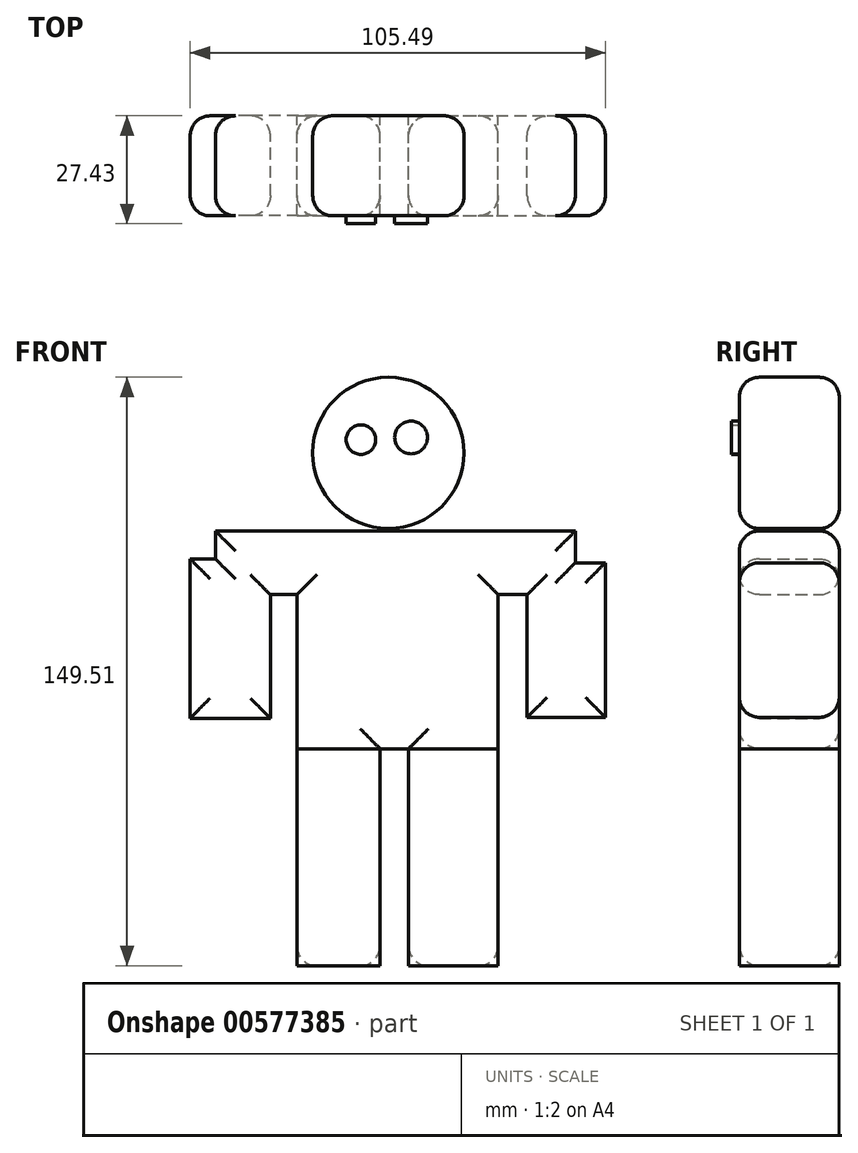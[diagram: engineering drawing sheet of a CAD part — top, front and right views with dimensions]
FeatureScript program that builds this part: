
annotation { "Feature Type Name" : "Feature", "Feature Type Description" : "" }
export const myFeature = defineFeature(function(context is Context, id is Id, definition is map)
    precondition{}
    {
        {
            var Q0;
            Q0=qCreatedBy(makeId("Front.planeOp"),FACE);
            var sketch = newSketch(context, id + "F0", { "sketchPlane" : qUnion([Q0])});
            skLineSegment(sketch, "E0.bottom", {"start": v(-23.26, 0) * mm, "end": v(-2.1, 0) * mm});
            skLineSegment(sketch, "E0.top", {"start": v(-23.26, -55.12) * mm, "end": v(-2.1, -55.12) * mm});
            skLineSegment(sketch, "E0.left", {"start": v(-23.26, 0) * mm, "end": v(-23.26, -55.12) * mm});
            skLineSegment(sketch, "E0.right", {"start": v(-2.1, 0) * mm, "end": v(-2.1, -55.12) * mm});
            skLineSegment(sketch, "E1.bottom", {"start": v(5.12, 0) * mm, "end": v(27.91, 0) * mm});
            skLineSegment(sketch, "E1.top", {"start": v(5.12, -55.12) * mm, "end": v(27.91, -55.12) * mm});
            skLineSegment(sketch, "E1.left", {"start": v(5.12, 0) * mm, "end": v(5.12, -55.12) * mm});
            skLineSegment(sketch, "E1.right", {"start": v(27.91, 0) * mm, "end": v(27.91, -55.12) * mm});
            skLineSegment(sketch, "E2.bottom", {"start": v(-23.26, 0) * mm, "end": v(27.91, 0) * mm});
            skLineSegment(sketch, "E2.top", {"start": v(-23.26, 55.36) * mm, "end": v(27.91, 55.36) * mm});
            skLineSegment(sketch, "E2.left", {"start": v(-23.26, 0) * mm, "end": v(-23.26, 55.36) * mm});
            skLineSegment(sketch, "E2.right", {"start": v(27.91, 0) * mm, "end": v(27.91, 55.36) * mm});
            skLineSegment(sketch, "E3.bottom", {"start": v(27.91, 55.36) * mm, "end": v(47.5, 55.36) * mm});
            skLineSegment(sketch, "E3.top", {"start": v(27.91, 39.15) * mm, "end": v(47.5, 39.15) * mm});
            skLineSegment(sketch, "E3.left", {"start": v(27.91, 55.36) * mm, "end": v(27.91, 39.15) * mm});
            skLineSegment(sketch, "E3.right", {"start": v(47.5, 55.36) * mm, "end": v(47.5, 39.15) * mm});
            skPoint(sketch, "E4.firstSnap0", {"position": v(27.91, 47.25) * mm});
            skLineSegment(sketch, "E4.bottom", {"start": v(35.27, 47.25) * mm, "end": v(55.13, 47.25) * mm});
            skLineSegment(sketch, "E4.top", {"start": v(35.27, 8) * mm, "end": v(55.13, 8) * mm});
            skLineSegment(sketch, "E4.left", {"start": v(35.27, 47.25) * mm, "end": v(35.27, 8) * mm});
            skLineSegment(sketch, "E4.right", {"start": v(55.13, 47.25) * mm, "end": v(55.13, 8) * mm});
            skLineSegment(sketch, "E5.bottom", {"start": v(-23.26, 55.36) * mm, "end": v(-43.94, 55.36) * mm});
            skLineSegment(sketch, "E5.top", {"start": v(-23.26, 39.15) * mm, "end": v(-43.94, 39.15) * mm});
            skLineSegment(sketch, "E5.left", {"start": v(-23.26, 55.36) * mm, "end": v(-23.26, 39.15) * mm});
            skLineSegment(sketch, "E5.right", {"start": v(-43.94, 55.36) * mm, "end": v(-43.94, 39.15) * mm});
            skLineSegment(sketch, "E6.bottom", {"start": v(-29.97, 48.24) * mm, "end": v(-50.36, 48.24) * mm});
            skLineSegment(sketch, "E6.top", {"start": v(-29.97, 7.77) * mm, "end": v(-50.36, 7.77) * mm});
            skLineSegment(sketch, "E6.left", {"start": v(-29.97, 48.24) * mm, "end": v(-29.97, 7.77) * mm});
            skLineSegment(sketch, "E6.right", {"start": v(-50.36, 48.24) * mm, "end": v(-50.36, 7.77) * mm});
            skSolve(sketch);
        }
        {
            var Q0;
            Q0=makeQuery(id+"F0.imprint","IMPRINT",FACE,{"disambiguationData":[TD([[makeQuery(id+"F0.imprint","IMPRINT",EDGE,{"derivedFrom":sQuery(id+"F0.wireOp",EDGE,"E0.top")}),1.0]])]});
            var Q1;
            Q1=makeQuery(id+"F0.imprint","IMPRINT",FACE,{"disambiguationData":[TD([[makeQuery(id+"F0.imprint","IMPRINT",EDGE,{"derivedFrom":sQuery(id+"F0.wireOp",EDGE,"E1.top")}),1.0]])]});
            extrude(context, id + "F1", {"entities" : qUnion([Q0, Q1]), "depth" : 25.4 * mm, "offsetDistance" : 25.4 * mm});
        }
        {
            var Q0;
            Q0 = qSketchRegion(id + "F0", true);
            extrude(context, id + "F2", {"entities" : qUnion([Q0]), "depth" : 25.4 * mm, "offsetDistance" : 25.4 * mm});
        }
        {
            var Q0;
            Q0=makeQuery(id+"F2.opExtrude","SWEPT_FACE",FACE,{"disambiguationData":[OSD([sQuery(id+"F0.wireOp",EDGE,"E1.top")])]});
            var Q1;
            Q1=makeQuery(id+"F2.opExtrude","SWEPT_FACE",FACE,{"disambiguationData":[OSD([sQuery(id+"F0.wireOp",EDGE,"E0.top")])]});
            var Q2;
            Q2=makeQuery(id+"F2.opExtrude","CAP_FACE",FACE,{"disambiguationData":[OSD([sQuery(id+"F0.wireOp",EDGE,"E0.top"),sQuery(id+"F0.wireOp",EDGE,"E0.left"),sQuery(id+"F0.wireOp",EDGE,"E0.right"),sQuery(id+"F0.wireOp",EDGE,"E1.top"),sQuery(id+"F0.wireOp",EDGE,"E1.left"),sQuery(id+"F0.wireOp",EDGE,"E1.right"),sQuery(id+"F0.wireOp",EDGE,"E2.bottom"),sQuery(id+"F0.wireOp",EDGE,"E2.top"),sQuery(id+"F0.wireOp",EDGE,"E2.left"),sQuery(id+"F0.wireOp",EDGE,"E2.right"),sQuery(id+"F0.wireOp",EDGE,"E3.bottom"),sQuery(id+"F0.wireOp",EDGE,"E3.top"),sQuery(id+"F0.wireOp",EDGE,"E3.right"),sQuery(id+"F0.wireOp",EDGE,"E4.bottom"),sQuery(id+"F0.wireOp",EDGE,"E4.top"),sQuery(id+"F0.wireOp",EDGE,"E4.left"),sQuery(id+"F0.wireOp",EDGE,"E4.right"),sQuery(id+"F0.wireOp",EDGE,"E5.bottom"),sQuery(id+"F0.wireOp",EDGE,"E5.top"),sQuery(id+"F0.wireOp",EDGE,"E5.right"),sQuery(id+"F0.wireOp",EDGE,"E6.bottom"),sQuery(id+"F0.wireOp",EDGE,"E6.top"),sQuery(id+"F0.wireOp",EDGE,"E6.left"),sQuery(id+"F0.wireOp",EDGE,"E6.right")])],"isStart":true});
            var Q3;
            Q3=makeQuery(id+"F2.opExtrude","CAP_FACE",FACE,{"disambiguationData":[OSD([sQuery(id+"F0.wireOp",EDGE,"E0.top"),sQuery(id+"F0.wireOp",EDGE,"E0.left"),sQuery(id+"F0.wireOp",EDGE,"E0.right"),sQuery(id+"F0.wireOp",EDGE,"E1.top"),sQuery(id+"F0.wireOp",EDGE,"E1.left"),sQuery(id+"F0.wireOp",EDGE,"E1.right"),sQuery(id+"F0.wireOp",EDGE,"E2.bottom"),sQuery(id+"F0.wireOp",EDGE,"E2.top"),sQuery(id+"F0.wireOp",EDGE,"E2.left"),sQuery(id+"F0.wireOp",EDGE,"E2.right"),sQuery(id+"F0.wireOp",EDGE,"E3.bottom"),sQuery(id+"F0.wireOp",EDGE,"E3.top"),sQuery(id+"F0.wireOp",EDGE,"E3.right"),sQuery(id+"F0.wireOp",EDGE,"E4.bottom"),sQuery(id+"F0.wireOp",EDGE,"E4.top"),sQuery(id+"F0.wireOp",EDGE,"E4.left"),sQuery(id+"F0.wireOp",EDGE,"E4.right"),sQuery(id+"F0.wireOp",EDGE,"E5.bottom"),sQuery(id+"F0.wireOp",EDGE,"E5.top"),sQuery(id+"F0.wireOp",EDGE,"E5.right"),sQuery(id+"F0.wireOp",EDGE,"E6.bottom"),sQuery(id+"F0.wireOp",EDGE,"E6.top"),sQuery(id+"F0.wireOp",EDGE,"E6.left"),sQuery(id+"F0.wireOp",EDGE,"E6.right")])],"isStart":false});
            fillet(context, id + "F3", {"entities" : qUnion([Q0, Q1, Q2, Q3]), "radius" : 5.08 * mm, "tangentPropagation" : true, "allowEdgeOverflow" : false});
        }
        {
            var Q0;
            Q0=makeQuery(id+"F2.opExtrude","CAP_FACE",FACE,{"disambiguationData":[OSD([sQuery(id+"F0.wireOp",EDGE,"E0.top"),sQuery(id+"F0.wireOp",EDGE,"E0.left"),sQuery(id+"F0.wireOp",EDGE,"E0.right"),sQuery(id+"F0.wireOp",EDGE,"E1.top"),sQuery(id+"F0.wireOp",EDGE,"E1.left"),sQuery(id+"F0.wireOp",EDGE,"E1.right"),sQuery(id+"F0.wireOp",EDGE,"E2.bottom"),sQuery(id+"F0.wireOp",EDGE,"E2.top"),sQuery(id+"F0.wireOp",EDGE,"E2.left"),sQuery(id+"F0.wireOp",EDGE,"E2.right")])],"isStart":true});
            var sketch = newSketch(context, id + "F4", { "sketchPlane" : qUnion([Q0])});
            skCircle(sketch, "E7", {"center": v(0, 75.17) * mm, "radius": 19.22 * mm});
            skSolve(sketch);
        }
        {
            var Q0;
            Q0=makeQuery(id+"F4.imprint","IMPRINT",FACE,{"disambiguationData":[TD([[makeQuery(id+"F4.imprint","IMPRINT",EDGE,{"derivedFrom":sQuery(id+"F4.wireOp",EDGE,"E7")}),1.0]])]});
            extrude(context, id + "F5", {"entities" : qUnion([Q0]), "oppositeDirection" : true, "depth" : 25.4 * mm, "offsetDistance" : 25.4 * mm});
        }
        {
            var Q0;
            Q0=makeQuery(id+"F5.opExtrude","CAP_FACE",FACE,{"disambiguationData":[OSD([sQuery(id+"F4.wireOp",EDGE,"E7")])],"isStart":false});
            var Q1;
            Q1=makeQuery(id+"F5.opExtrude","CAP_FACE",FACE,{"disambiguationData":[OSD([sQuery(id+"F4.wireOp",EDGE,"E7")])],"isStart":true});
            var Q2;
            Q2=makeQuery(id+"F5.opExtrude","SWEPT_FACE",FACE,{"disambiguationData":[OSD([sQuery(id+"F4.wireOp",EDGE,"E7")])]});
            fillet(context, id + "F6", {"entities" : qUnion([Q0, Q1, Q2]), "radius" : 5.08 * mm, "tangentPropagation" : true, "allowEdgeOverflow" : false});
        }
        {
            var Q0;
            Q0=makeQuery(id+"F5.opExtrude","CAP_FACE",FACE,{"disambiguationData":[OSD([sQuery(id+"F4.wireOp",EDGE,"E7")])],"isStart":false});
            var sketch = newSketch(context, id + "F7", { "sketchPlane" : qUnion([Q0])});
            skCircle(sketch, "E8", {"center": v(-6.97, 78.53) * mm, "radius": 3.74 * mm});
            skCircle(sketch, "E9", {"center": v(5.78, 79.1) * mm, "radius": 4.16 * mm});
            skSolve(sketch);
        }
        {
            var Q0;
            Q0=makeQuery(id+"F7.imprint","IMPRINT",FACE,{"disambiguationData":[TD([[makeQuery(id+"F7.imprint","IMPRINT",EDGE,{"derivedFrom":sQuery(id+"F7.wireOp",EDGE,"E8")}),1.0]])]});
            var Q1;
            Q1=makeQuery(id+"F7.imprint","IMPRINT",FACE,{"disambiguationData":[TD([[makeQuery(id+"F7.imprint","IMPRINT",EDGE,{"derivedFrom":sQuery(id+"F7.wireOp",EDGE,"E9")}),1.0]])]});
            extrude(context, id + "F8", {"entities" : qUnion([Q0, Q1]), "operationType" : NewBodyOperationType.ADD, "depth" : 2.03 * mm, "offsetDistance" : 25.4 * mm});
        }
    });
